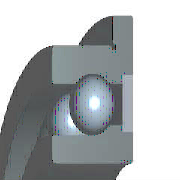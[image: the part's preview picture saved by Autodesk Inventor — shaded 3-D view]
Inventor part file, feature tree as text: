
AUTODESK INVENTOR PART (.ipt)
format: ipt  version: 2022 (Build 260153000, 153)  size: 349,184 bytes
history: native  units: mm (DEFAULTED — no unit token found)
features: other x2, pattern_circular x1, extrude x1, sketch x1
ambient origin geometry x8: Origin, YZ Plane, XZ Plane, XY Plane, X Axis, Y Axis, Z Axis, Center Point
bodies: Solid1 (feature_tree), Body (feature_tree)
feature tree (5):
  other  "Ball"
  pattern_circular  "Balls"  [2 undecoded]
  other  "Ring1"
  extrude  "Indent1"  Depth=5.0mm
  sketch  "Sketch2"  dims[d0=0.0mm d3=5.46mm d4=9.0mm d5=19.5mm d6=30.0mm d7=30.0mm d103=90.0deg d104=90.0deg d8=60.0mm d9=360.0deg d10=0.25mm d11=0.6mm d12=0.6mm d13=0.3mm d16=0.0mm d17=0.0mm d19=15.0537mm d20=24.3117mm d21=1.25mm d127=90.0deg d22=15.0537mm d23=24.3117mm d24=0.02mm d25=0.0mm d26=1.827mm d27=3.36mm d28=10.0mm d29=5.0mm d145=0.0mm d146=0.0mm]
note: 2 required parameter values undecoded (feature->parameter linkage not recoverable at this tier; creation-order binding heuristic only, values carry confidence <= 0.55)
